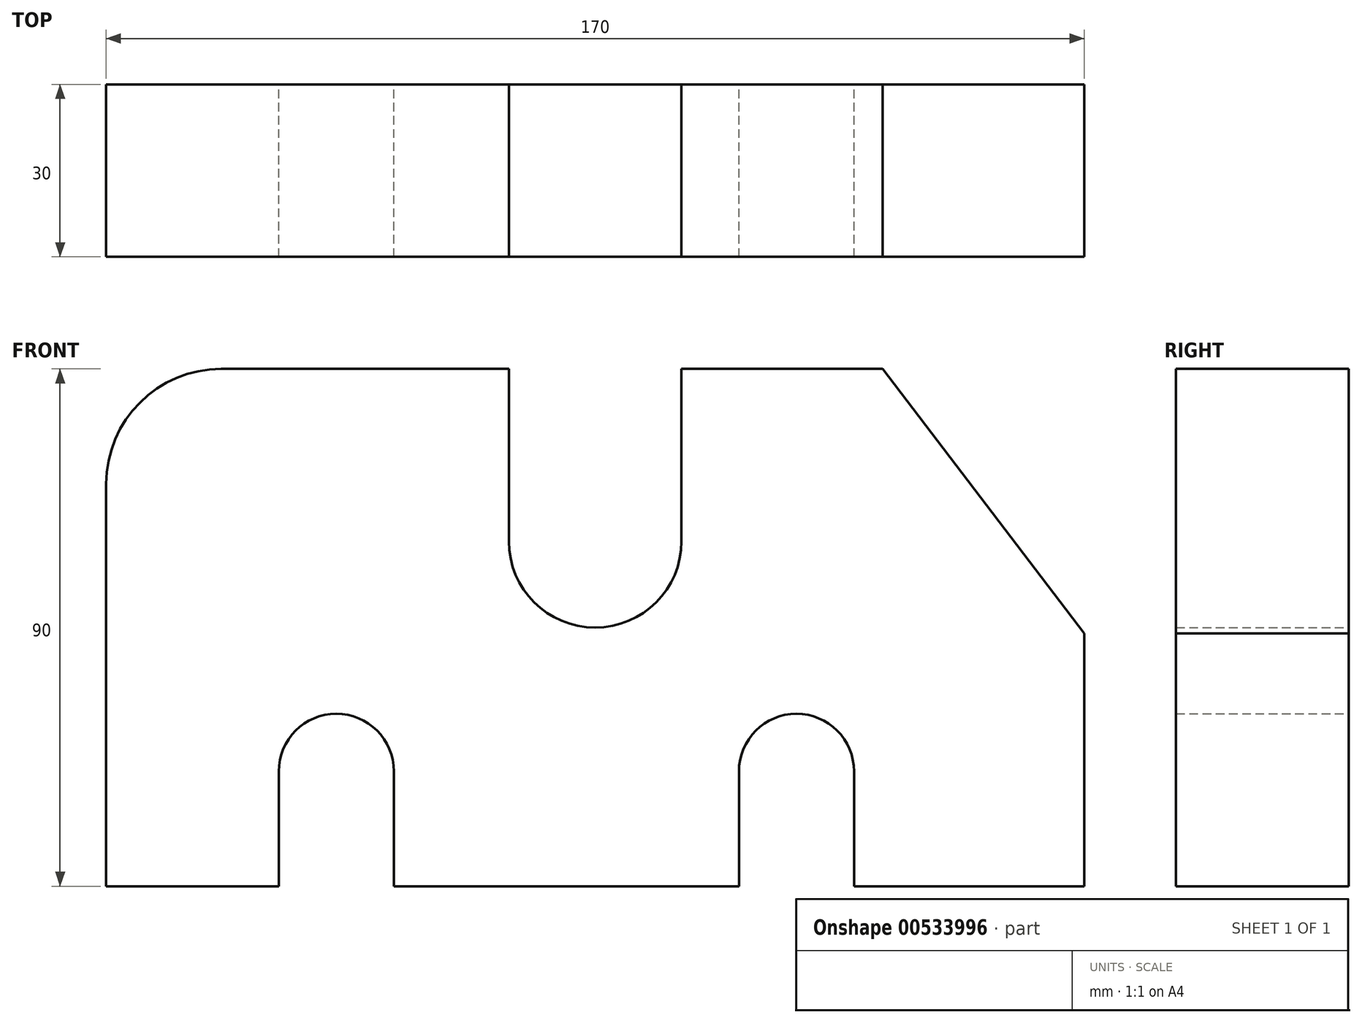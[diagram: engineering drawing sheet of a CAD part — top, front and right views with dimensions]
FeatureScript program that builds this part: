
annotation { "Feature Type Name" : "Feature", "Feature Type Description" : "" }
export const myFeature = defineFeature(function(context is Context, id is Id, definition is map)
    precondition{}
    {
        {
            var Q0;
            Q0=qCreatedBy(makeId("Front.planeOp"),FACE);
            var sketch = newSketch(context, id + "F0", { "sketchPlane" : qUnion([Q0])});
            skLineSegment(sketch, "E0", {"start": v(-100, -39.45) * mm, "end": v(-70, -39.45) * mm});
            skLineSegment(sketch, "E1", {"start": v(-70, -39.45) * mm, "end": v(-70, -19.45) * mm});
            skLineSegment(sketch, "E2", {"start": v(-60, -9.45) * mm, "end": v(-60, -9.45) * mm});
            skLineSegment(sketch, "E3", {"start": v(-50, -19.45) * mm, "end": v(-50, -39.45) * mm});
            skLineSegment(sketch, "E4", {"start": v(-50, -39.45) * mm, "end": v(10, -39.45) * mm});
            skLineSegment(sketch, "E5", {"start": v(10, -39.45) * mm, "end": v(10, -19.45) * mm});
            skLineSegment(sketch, "E6", {"start": v(20, -9.45) * mm, "end": v(20, -9.45) * mm});
            skLineSegment(sketch, "E7", {"start": v(30, -19.45) * mm, "end": v(30, -39.45) * mm});
            skLineSegment(sketch, "E8", {"start": v(30, -39.45) * mm, "end": v(70, -39.45) * mm});
            skLineSegment(sketch, "E9", {"start": v(70, -39.45) * mm, "end": v(70, 4.55) * mm});
            skLineSegment(sketch, "E10", {"start": v(70, 4.55) * mm, "end": v(35, 50.55) * mm});
            skLineSegment(sketch, "E11", {"start": v(35, 50.55) * mm, "end": v(0, 50.55) * mm});
            skLineSegment(sketch, "E12", {"start": v(0, 50.55) * mm, "end": v(0, 20.55) * mm});
            skLineSegment(sketch, "E13", {"start": v(-30, 20.55) * mm, "end": v(-30, 50.55) * mm});
            skLineSegment(sketch, "E14", {"start": v(-30, 50.55) * mm, "end": v(-80, 50.55) * mm});
            skLineSegment(sketch, "E15", {"start": v(-100, 30.55) * mm, "end": v(-100, -39.45) * mm});
            skPoint(sketch, "E16.visualSharp", {"position": v(-100, 50.55) * mm});
            skArc(sketch, "E16.filletArc", {"start": v(-80, 50.55) * mm, "mid": v(-94.14, 44.7) * mm, "end": v(-100, 30.55) * mm});
            skPoint(sketch, "E17.visualSharp", {"position": v(-70, -9.45) * mm});
            skArc(sketch, "E17.filletArc", {"start": v(-60, -9.45) * mm, "mid": v(-67.07, -12.38) * mm, "end": v(-70, -19.45) * mm});
            skPoint(sketch, "E18.visualSharp", {"position": v(-50, -9.45) * mm});
            skArc(sketch, "E18.filletArc", {"start": v(-50, -19.45) * mm, "mid": v(-52.93, -12.38) * mm, "end": v(-60, -9.45) * mm});
            skPoint(sketch, "E19.visualSharp", {"position": v(10, -9.45) * mm});
            skArc(sketch, "E19.filletArc", {"start": v(20, -9.45) * mm, "mid": v(12.93, -12.38) * mm, "end": v(10, -19.45) * mm});
            skPoint(sketch, "E20.visualSharp", {"position": v(30, -9.45) * mm});
            skArc(sketch, "E20.filletArc", {"start": v(30, -19.45) * mm, "mid": v(27.07, -12.38) * mm, "end": v(20, -9.45) * mm});
            skPoint(sketch, "E21.visualSharp", {"position": v(-30, 20.55) * mm});
            skPoint(sketch, "E22.visualSharp", {"position": v(0, 20.55) * mm});
            skArc(sketch, "E23", {"start": v(-30, 20.55) * mm, "mid": v(-15, 5.55) * mm, "end": v(0, 20.55) * mm});
            skSolve(sketch);
        }
        {
            var Q0;
            Q0 = qSketchRegion(id + "F0", true);
            extrude(context, id + "F1", {"entities" : qUnion([Q0]), "depth" : 30 * mm, "offsetDistance" : 25 * mm});
        }
    });
